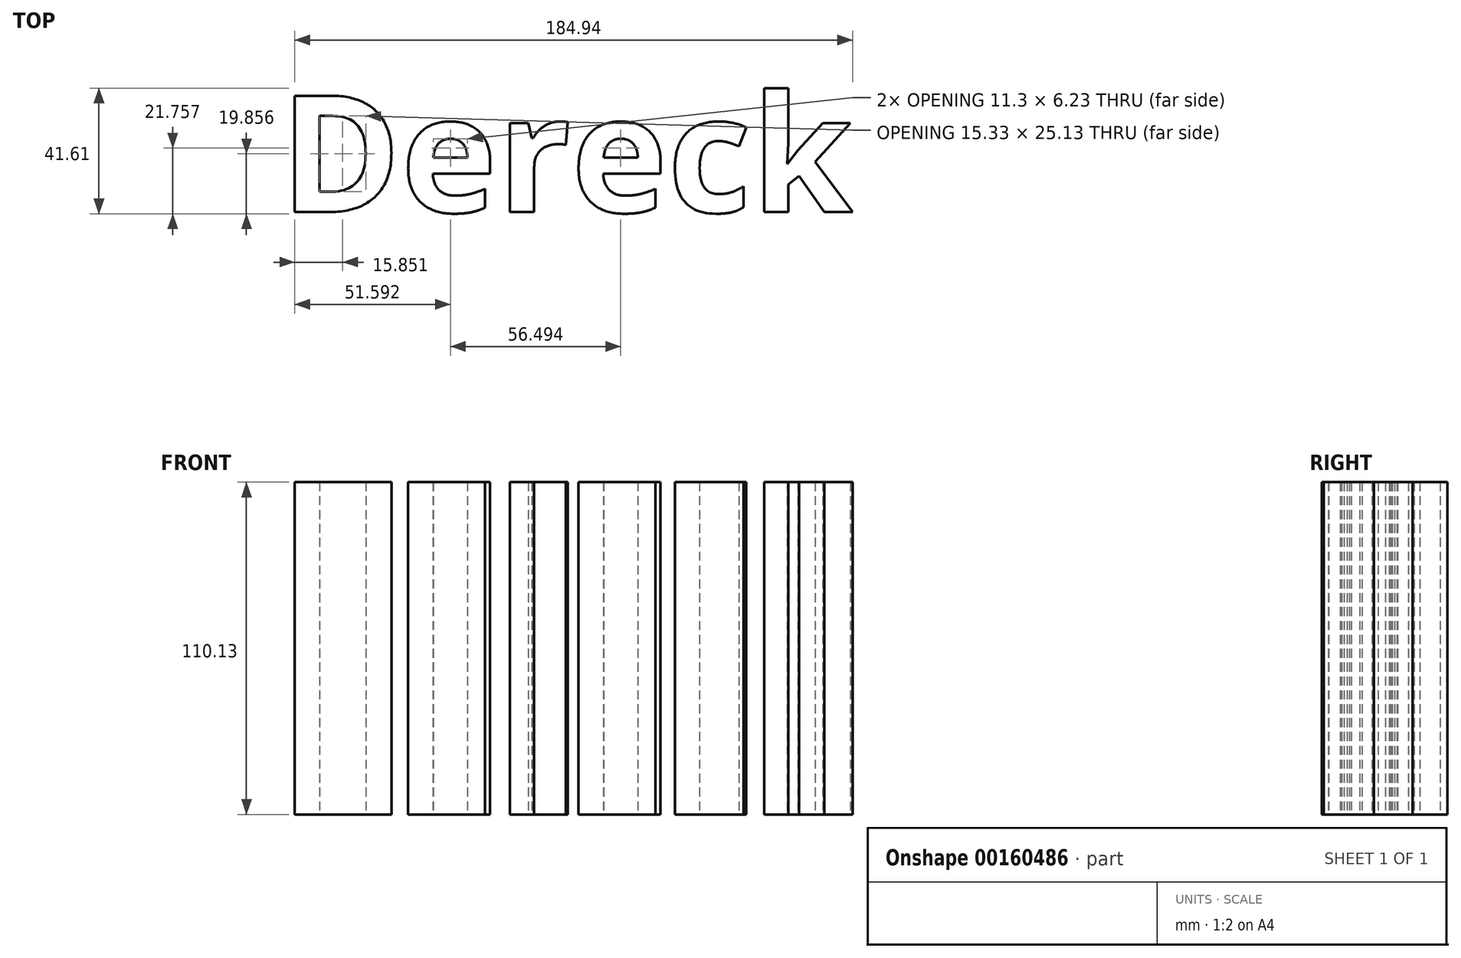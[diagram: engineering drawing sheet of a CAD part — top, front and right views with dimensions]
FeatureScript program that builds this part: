
annotation { "Feature Type Name" : "Feature", "Feature Type Description" : "" }
export const myFeature = defineFeature(function(context is Context, id is Id, definition is map)
    precondition{}
    {
        {
            var Q0;
            Q0=qCreatedBy(makeId("Top.planeOp"),FACE);
            var sketch = newSketch(context, id + "F1", { "sketchPlane" : qUnion([Q0])});
            skText(sketch, "E0", { "text": "Dereck", "fontName": "OpenSans-Bold.ttf"});
            const initialGuessFvwlFoYBfAgN33ijR_0  = {"E0": [0, 0, 1, 0, 0.03893]};
            skSetInitialGuess(sketch, initialGuessFvwlFoYBfAgN33ijR_0);
            skSolve(sketch);
        }
        {
            var Q0;
            Q0 = qSketchRegion(id + "F1", true);
            extrude(context, id + "F0", {"entities" : qUnion([Q0]), "depth" : 110.13 * mm});
        }
    });
